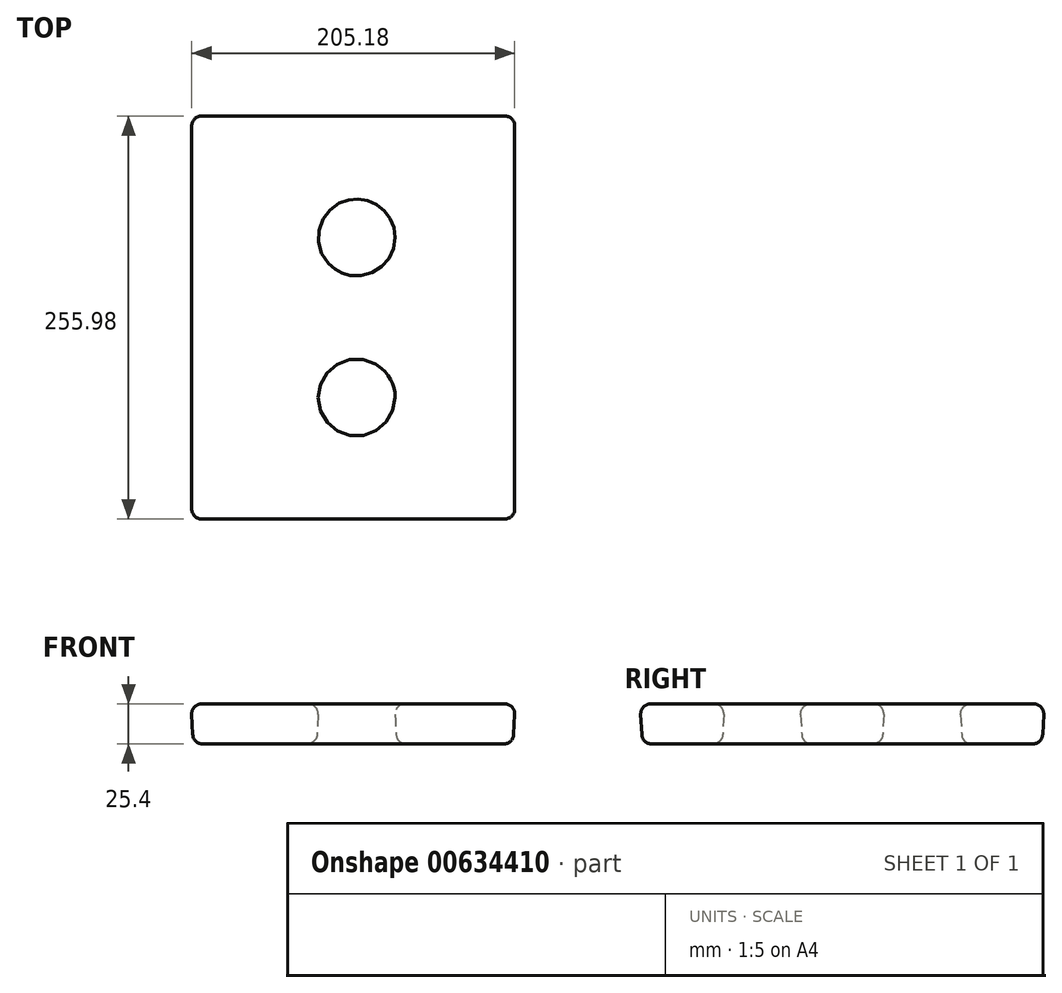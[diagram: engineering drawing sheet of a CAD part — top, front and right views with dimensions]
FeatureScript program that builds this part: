
annotation { "Feature Type Name" : "Feature", "Feature Type Description" : "" }
export const myFeature = defineFeature(function(context is Context, id is Id, definition is map)
    precondition{}
    {
        {
            var Q0;
            Q0=qCreatedBy(makeId("Top.planeOp"),FACE);
            var sketch = newSketch(context, id + "F0", { "sketchPlane" : qUnion([Q0])});
            skLineSegment(sketch, "E0.bottom", {"start": v(0, 0) * mm, "end": v(203.2, 0) * mm});
            skLineSegment(sketch, "E0.top", {"start": v(0, 254) * mm, "end": v(203.2, 254) * mm});
            skLineSegment(sketch, "E0.left", {"start": v(0, 0) * mm, "end": v(0, 254) * mm});
            skLineSegment(sketch, "E0.right", {"start": v(203.2, 0) * mm, "end": v(203.2, 254) * mm});
            skCircle(sketch, "E1", {"center": v(103.78, 177.8) * mm, "radius": 25.4 * mm});
            skLineSegment(sketch, "E2", {"start": v(0, 127) * mm, "end": v(203.2, 127) * mm, "construction": true});
            skCircle(sketch, "E3.MirrorC", {"center": v(103.78, 76.2) * mm, "radius": 25.4 * mm});
            skSolve(sketch);
        }
        {
            var Q0;
            Q0=makeQuery(id+"F0.imprint","IMPRINT",FACE,{"disambiguationData":[TD([[makeQuery(id+"F0.imprint","IMPRINT",EDGE,{"derivedFrom":sQuery(id+"F0.wireOp",EDGE,"E0.bottom")}),1.0]])]});
            extrude(context, id + "F1", {"entities" : qUnion([Q0]), "depth" : 25.4 * mm, "offsetDistance" : 25.4 * mm, "hasDraft" : true, "draftAngle" : 3 * degree});
        }
        {
            var Q0;
            Q0=makeQuery(id+"F1.opExtrude","CAP_EDGE",EDGE,{"disambiguationData":[OSD([sQuery(id+"F0.wireOp",EDGE,"E0.left")])],"isStart":true});
            var Q1;
            Q1=makeQuery(id+"F1.opExtrude","CAP_EDGE",EDGE,{"disambiguationData":[OSD([sQuery(id+"F0.wireOp",EDGE,"E0.left")])],"isStart":false});
            var Q2;
            Q2=makeQuery(id+"F1.opExtrude","SWEPT_EDGE",EDGE,{"disambiguationData":[OSD([sQuery(id+"F0.wireOp",EDGE,"E0.top"),sQuery(id+"F0.wireOp",EDGE,"E0.left")])]});
            var Q3;
            Q3=makeQuery(id+"F1.opExtrude","CAP_EDGE",EDGE,{"disambiguationData":[OSD([sQuery(id+"F0.wireOp",EDGE,"E0.top")])],"isStart":false});
            var Q4;
            Q4=makeQuery(id+"F1.opExtrude","CAP_EDGE",EDGE,{"disambiguationData":[OSD([sQuery(id+"F0.wireOp",EDGE,"E1")])],"isStart":false});
            var Q5;
            Q5=makeQuery(id+"F1.opExtrude","CAP_EDGE",EDGE,{"disambiguationData":[OSD([sQuery(id+"F0.wireOp",EDGE,"E1")])],"isStart":true});
            var Q6;
            Q6=makeQuery(id+"F1.opExtrude","SWEPT_FACE",FACE,{"disambiguationData":[OSD([sQuery(id+"F0.wireOp",EDGE,"E1")])]});
            var Q7;
            Q7=makeQuery(id+"F1.opExtrude","SWEPT_EDGE",EDGE,{"disambiguationData":[OSD([sQuery(id+"F0.wireOp",EDGE,"E0.bottom"),sQuery(id+"F0.wireOp",EDGE,"E0.left")])]});
            var Q8;
            Q8=makeQuery(id+"F1.opExtrude","CAP_EDGE",EDGE,{"disambiguationData":[OSD([sQuery(id+"F0.wireOp",EDGE,"E0.bottom")])],"isStart":false});
            var Q9;
            Q9=makeQuery(id+"F1.opExtrude","CAP_EDGE",EDGE,{"disambiguationData":[OSD([sQuery(id+"F0.wireOp",EDGE,"E0.right")])],"isStart":false});
            var Q10;
            Q10=makeQuery(id+"F1.opExtrude","CAP_EDGE",EDGE,{"disambiguationData":[OSD([sQuery(id+"F0.wireOp",EDGE,"E3.MirrorC")])],"isStart":false});
            var Q11;
            Q11=makeQuery(id+"F1.opExtrude","CAP_EDGE",EDGE,{"disambiguationData":[OSD([sQuery(id+"F0.wireOp",EDGE,"E3.MirrorC")])],"isStart":true});
            var Q12;
            Q12=makeQuery(id+"F1.opExtrude","SWEPT_FACE",FACE,{"disambiguationData":[OSD([sQuery(id+"F0.wireOp",EDGE,"E3.MirrorC")])]});
            var Q13;
            Q13=makeQuery(id+"F1.opExtrude","SWEPT_FACE",FACE,{"disambiguationData":[OSD([sQuery(id+"F0.wireOp",EDGE,"E0.bottom")])]});
            var Q14;
            Q14=makeQuery(id+"F1.opExtrude","CAP_EDGE",EDGE,{"disambiguationData":[OSD([sQuery(id+"F0.wireOp",EDGE,"E0.top")])],"isStart":true});
            var Q15;
            Q15=makeQuery(id+"F1.opExtrude","CAP_EDGE",EDGE,{"disambiguationData":[OSD([sQuery(id+"F0.wireOp",EDGE,"E0.right")])],"isStart":true});
            var Q16;
            Q16=makeQuery(id+"F1.opExtrude","SWEPT_EDGE",EDGE,{"disambiguationData":[OSD([sQuery(id+"F0.wireOp",EDGE,"E0.top"),sQuery(id+"F0.wireOp",EDGE,"E0.right")])]});
            fillet(context, id + "F2", {"entities" : qUnion([Q0, Q1, Q2, Q3, Q4, Q5, Q6, Q7, Q8, Q9, Q10, Q11, Q12, Q13, Q14, Q15, Q16]), "radius" : 6.35 * mm, "tangentPropagation" : true, "allowEdgeOverflow" : false});
        }
    });
